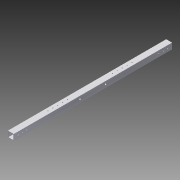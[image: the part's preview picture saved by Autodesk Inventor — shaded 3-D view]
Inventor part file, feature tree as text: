
AUTODESK INVENTOR PART (.ipt)
format: ipt  version: 2015 (Build 190159000, 159)  size: 169,984 bytes
history: native  units: in
note: dims shown in document units (in); Inventor stores cm internally (conversion verified against a paired STEP export)
features: other x4, hole x3, extrude x1
ambient origin geometry x8: Origin, YZ Plane, XZ Plane, XY Plane, X Axis, Y Axis, Z Axis, Center Point
bodies: Solid1 (feature_tree)
feature tree (8):
  extrude  "profile_extrusion"  Depth=1.0in
  hole  "gbmh"  [1 undecoded]
  hole  "side_rivet_holes"  [1 undecoded]
  hole  "tb_rivet_holes"  [1 undecoded]
  other  "profile_sketch"
  other  "gbmh_sketch"
  other  "side_rivet_holes_sketch"
  other  "crossbar_rivet_holes_sketch"
note: 3 required parameter values undecoded (feature->parameter linkage not recoverable at this tier; creation-order binding heuristic only, values carry confidence <= 0.55)
